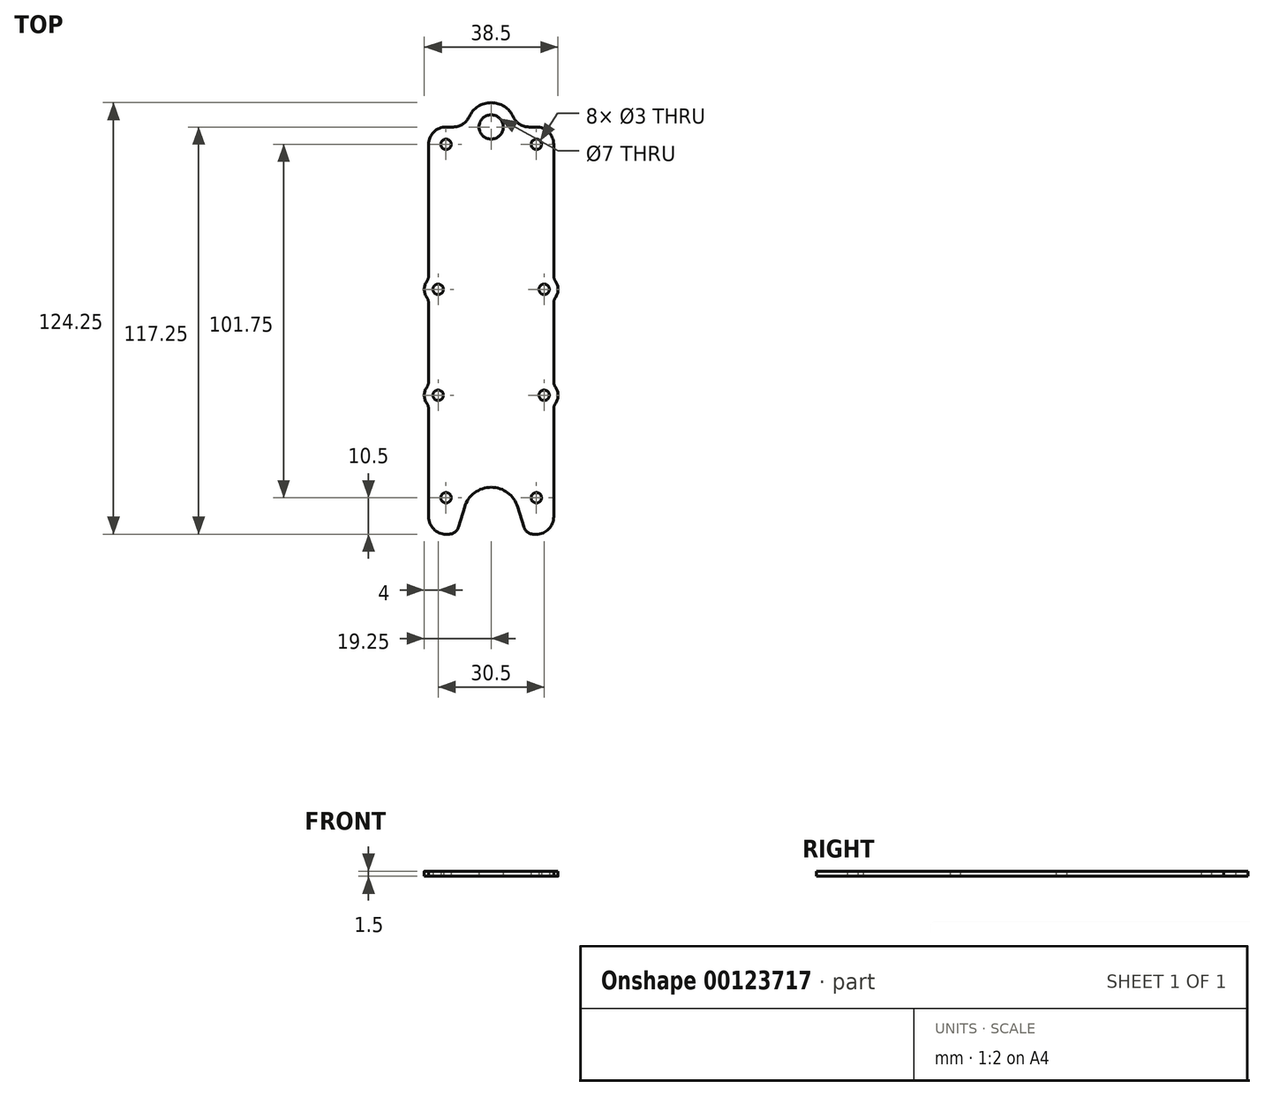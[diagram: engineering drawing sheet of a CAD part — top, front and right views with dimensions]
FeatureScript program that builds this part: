
annotation { "Feature Type Name" : "Feature", "Feature Type Description" : "" }
export const myFeature = defineFeature(function(context is Context, id is Id, definition is map)
    precondition{}
    {
        {
            var Q0;
            Q0=qCreatedBy(makeId("Top.planeOp"),FACE);
            var sketch = newSketch(context, id + "F0", { "sketchPlane" : qUnion([Q0])});
            skCircle(sketch, "E0", {"center": v(-13, -44.75) * mm, "radius": 1.5 * mm});
            skCircle(sketch, "E1", {"center": v(13, -44.75) * mm, "radius": 1.5 * mm});
            skLineSegment(sketch, "E2", {"start": v(-13, -44.75) * mm, "end": v(13, -44.75) * mm, "construction": true});
            skCircle(sketch, "E3", {"center": v(-15.25, 15.25) * mm, "radius": 1.5 * mm});
            skCircle(sketch, "E4.0.1.0", {"center": v(-15.25, -15.25) * mm, "radius": 1.5 * mm});
            skCircle(sketch, "E4.1.0.0", {"center": v(15.25, 15.25) * mm, "radius": 1.5 * mm});
            skCircle(sketch, "E4.1.1.0", {"center": v(15.25, -15.25) * mm, "radius": 1.5 * mm});
            skLineSegment(sketch, "E4.direction1", {"start": v(-15.25, 15.25) * mm, "end": v(15.25, 15.25) * mm, "construction": true});
            skLineSegment(sketch, "E4.direction2", {"start": v(-15.25, 15.25) * mm, "end": v(-15.25, -15.25) * mm, "construction": true});
            skLineSegment(sketch, "E5", {"start": v(-18, 57) * mm, "end": v(-18, 18.15) * mm});
            skLineSegment(sketch, "E6", {"start": v(18, 57) * mm, "end": v(18, 18.15) * mm});
            skLineSegment(sketch, "E7", {"start": v(-13, -55.25) * mm, "end": v(-10, -55.25) * mm});
            skLineSegment(sketch, "E8", {"start": v(13, -55.25) * mm, "end": v(10, -55.25) * mm});
            skArc(sketch, "E9", {"start": v(7.66, -47.45) * mm, "mid": v(0, -41.75) * mm, "end": v(-7.66, -47.45) * mm});
            skLineSegment(sketch, "E10", {"start": v(-10, -55.25) * mm, "end": v(-7.66, -47.45) * mm});
            skLineSegment(sketch, "E11", {"start": v(10, -55.25) * mm, "end": v(7.66, -47.45) * mm});
            skLineSegment(sketch, "E12", {"start": v(-13, 62) * mm, "end": v(-10.9, 62) * mm});
            skCircle(sketch, "E13", {"center": v(-13, 57) * mm, "radius": 1.5 * mm});
            skCircle(sketch, "E14", {"center": v(13, 57) * mm, "radius": 1.5 * mm});
            skArc(sketch, "E15", {"start": v(-18, -12.35) * mm, "mid": v(-19.25, -15.25) * mm, "end": v(-18, -18.15) * mm});
            skArc(sketch, "E16", {"start": v(18, -18.15) * mm, "mid": v(19.25, -15.25) * mm, "end": v(18, -12.35) * mm});
            skArc(sketch, "E17", {"start": v(18, 12.35) * mm, "mid": v(19.25, 15.25) * mm, "end": v(18, 18.15) * mm});
            skArc(sketch, "E18", {"start": v(-18, 18.15) * mm, "mid": v(-19.25, 15.25) * mm, "end": v(-18, 12.35) * mm});
            skLineSegment(sketch, "E19.trimOffspring", {"start": v(-18, 12.35) * mm, "end": v(-18, -12.35) * mm});
            skLineSegment(sketch, "E20.trimOffspring", {"start": v(-18, -18.15) * mm, "end": v(-18, -50.25) * mm});
            skLineSegment(sketch, "E21.trimOffspring", {"start": v(18, -18.15) * mm, "end": v(18, -50.25) * mm});
            skLineSegment(sketch, "E22.trimOffspring", {"start": v(18, 12.35) * mm, "end": v(18, -12.35) * mm});
            skPoint(sketch, "E23.visualSharp", {"position": v(-18, 62) * mm});
            skArc(sketch, "E23.filletArc", {"start": v(-13, 62) * mm, "mid": v(-16.54, 60.54) * mm, "end": v(-18, 57) * mm});
            skPoint(sketch, "E24.visualSharp", {"position": v(18, 62) * mm});
            skArc(sketch, "E24.filletArc", {"start": v(18, 57) * mm, "mid": v(16.54, 60.54) * mm, "end": v(13, 62) * mm});
            skPoint(sketch, "E25.visualSharp", {"position": v(-18, -55.25) * mm});
            skArc(sketch, "E25.filletArc", {"start": v(-18, -50.25) * mm, "mid": v(-16.54, -53.79) * mm, "end": v(-13, -55.25) * mm});
            skPoint(sketch, "E26.visualSharp", {"position": v(18, -55.25) * mm});
            skArc(sketch, "E26.filletArc", {"start": v(13, -55.25) * mm, "mid": v(16.54, -53.79) * mm, "end": v(18, -50.25) * mm});
            skCircle(sketch, "E27", {"center": v(0, 62) * mm, "radius": 3.5 * mm});
            skArc(sketch, "E28", {"start": v(6.36, 64.92) * mm, "mid": v(0, 69) * mm, "end": v(-6.36, 64.92) * mm});
            skLineSegment(sketch, "E29.trimOffspring", {"start": v(10.9, 62) * mm, "end": v(13, 62) * mm});
            skPoint(sketch, "E30.visualSharp", {"position": v(-7, 62) * mm});
            skArc(sketch, "E30.filletArc", {"start": v(-10.9, 62) * mm, "mid": v(-8.2, 62.8) * mm, "end": v(-6.36, 64.92) * mm});
            skPoint(sketch, "E31.visualSharp", {"position": v(7, 62) * mm});
            skArc(sketch, "E31.filletArc", {"start": v(6.36, 64.92) * mm, "mid": v(8.2, 62.8) * mm, "end": v(10.9, 62) * mm});
            skSolve(sketch);
        }
        {
            var Q0;
            Q0=qSketchRegion(id+"F0",true);
            extrude(context, id + "F1", {"entities" : qUnion([Q0]), "depth" : 1.5 * mm});
        }
        {
            var Q0;
            Q0=makeQuery(id+"F1.opExtrude","SWEPT_EDGE",EDGE,{"disambiguationData":[OSD([sQuery(id+"F0.wireOp",EDGE,"E18"),sQuery(id+"F0.wireOp",EDGE,"E19.trimOffspring")])]});
            var Q1;
            Q1=makeQuery(id+"F1.opExtrude","SWEPT_EDGE",EDGE,{"disambiguationData":[OSD([sQuery(id+"F0.wireOp",EDGE,"E5"),sQuery(id+"F0.wireOp",EDGE,"E18")])]});
            var Q2;
            Q2=makeQuery(id+"F1.opExtrude","SWEPT_EDGE",EDGE,{"disambiguationData":[OSD([sQuery(id+"F0.wireOp",EDGE,"E15"),sQuery(id+"F0.wireOp",EDGE,"E19.trimOffspring")])]});
            var Q3;
            Q3=makeQuery(id+"F1.opExtrude","SWEPT_EDGE",EDGE,{"disambiguationData":[OSD([sQuery(id+"F0.wireOp",EDGE,"E15"),sQuery(id+"F0.wireOp",EDGE,"E20.trimOffspring")])]});
            var Q4;
            Q4=makeQuery(id+"F1.opExtrude","SWEPT_EDGE",EDGE,{"disambiguationData":[OSD([sQuery(id+"F0.wireOp",EDGE,"E16"),sQuery(id+"F0.wireOp",EDGE,"E21.trimOffspring")])]});
            var Q5;
            Q5=makeQuery(id+"F1.opExtrude","SWEPT_EDGE",EDGE,{"disambiguationData":[OSD([sQuery(id+"F0.wireOp",EDGE,"E16"),sQuery(id+"F0.wireOp",EDGE,"E22.trimOffspring")])]});
            var Q6;
            Q6=makeQuery(id+"F1.opExtrude","SWEPT_EDGE",EDGE,{"disambiguationData":[OSD([sQuery(id+"F0.wireOp",EDGE,"E17"),sQuery(id+"F0.wireOp",EDGE,"E22.trimOffspring")])]});
            var Q7;
            Q7=makeQuery(id+"F1.opExtrude","SWEPT_EDGE",EDGE,{"disambiguationData":[OSD([sQuery(id+"F0.wireOp",EDGE,"E6"),sQuery(id+"F0.wireOp",EDGE,"E17")])]});
            var Q8;
            Q8=makeQuery(id+"F1.opExtrude","SWEPT_EDGE",EDGE,{"disambiguationData":[OSD([sQuery(id+"F0.wireOp",EDGE,"E7"),sQuery(id+"F0.wireOp",EDGE,"E10")])]});
            var Q9;
            Q9=makeQuery(id+"F1.opExtrude","SWEPT_EDGE",EDGE,{"disambiguationData":[OSD([sQuery(id+"F0.wireOp",EDGE,"E8"),sQuery(id+"F0.wireOp",EDGE,"E11")])]});
            fillet(context, id + "F2", {"entities" : qUnion([Q0, Q1, Q2, Q3, Q4, Q5, Q6, Q7, Q8, Q9]), "radius" : 3 * mm, "tangentPropagation" : true, "allowEdgeOverflow" : false});
        }
    });
